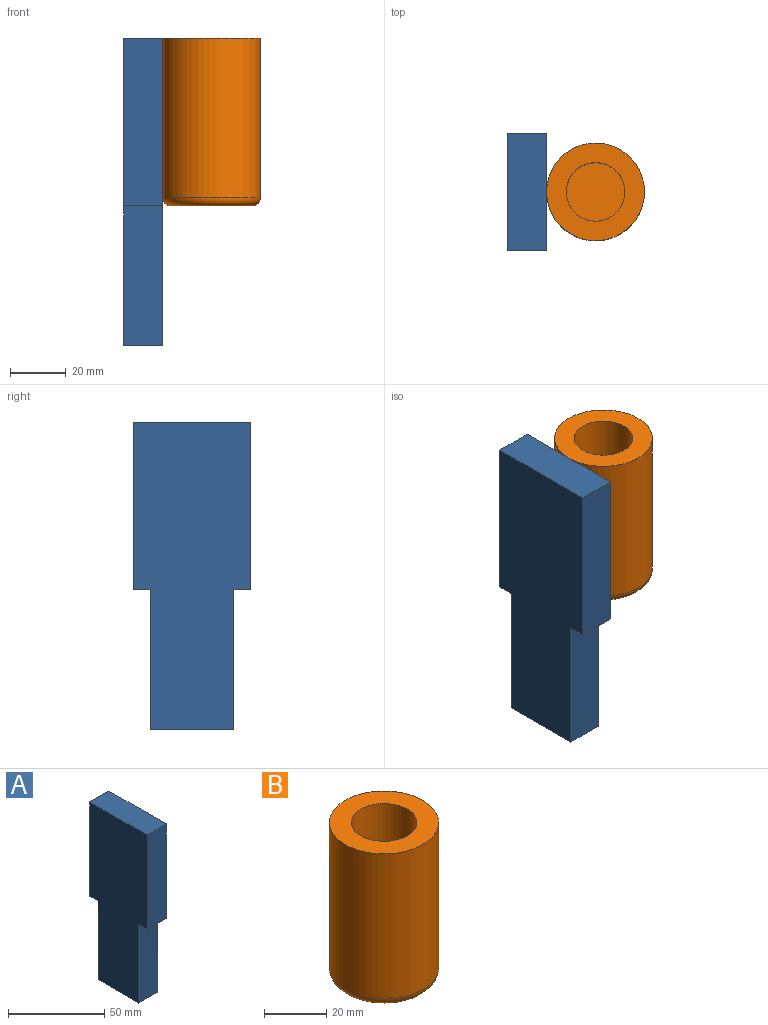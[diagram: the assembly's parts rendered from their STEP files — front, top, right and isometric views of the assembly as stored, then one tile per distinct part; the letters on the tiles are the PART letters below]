
ASSEMBLY  parts=2 mates=1
PART A: 10 faces, bbox 14x42x110 mm
  f0: plane 30x14mm, normal (0,0,-1), area 420mm2, adj f1,f7,f8,f9
  f1: plane 50x14mm, normal (0,1,0), area 700mm2, adj f0,f2,f8,f9
  f2: plane 14x6mm, normal (0,0,-1), area 84mm2, adj f1,f3,f8,f9
  f3: plane 60x14mm, normal (0,1,0), area 840mm2, adj f2,f4,f8,f9
  f4: plane 42x14mm, normal (0,0,1), area 588mm2, adj f3,f5,f8,f9
  f5: plane 60x14mm, normal (0,-1,0), area 840mm2, adj f4,f6,f8,f9
  f6: plane 14x6mm, normal (0,0,-1), area 84mm2, adj f5,f7,f8,f9
  f7: plane 50x14mm, normal (0,-1,0), area 700mm2, adj f0,f6,f8,f9
  f8: plane 110x42mm, normal (1,0,0), area 4020mm2, adj f0,f1,f2,f3,f4,f5,f6,f7
  f9: plane 110x42mm, normal (-1,0,0), area 4020mm2, adj f0,f1,f2,f3,f4,f5,f6,f7
PART B: 6 faces, bbox 37.9x37.9x60 mm
  f0: cylinder r=17.5mm len=57mm, axis (0,0,-1), area 6267.5mm2, adj f1,f3
  f1: plane 35x35mm, normal (0,0,1), area 615.8mm2, adj f0,f4
  f2: plane 29x29mm, normal (0,0,-1), area 660.5mm2, adj f3
  f3: torus R=14.5mm, axis (0,0,1), area 485.9mm2, adj f0,f2
  f4: cylinder r=10.5mm len=53mm, axis (0,0,-1), area 3496.6mm2, adj f1,f5
  f5: plane 21x21mm, normal (0,0,1), area 346.4mm2, adj f4
PLACE A t=(-32.8,-28.47,8.74)mm
PLACE B t=(-1.3,-28.47,-35.36)mm
MATE fastened B.f0 <-> A.f4  axis (0,0,-1) through (-1.3,-28.47,24.64)mm
